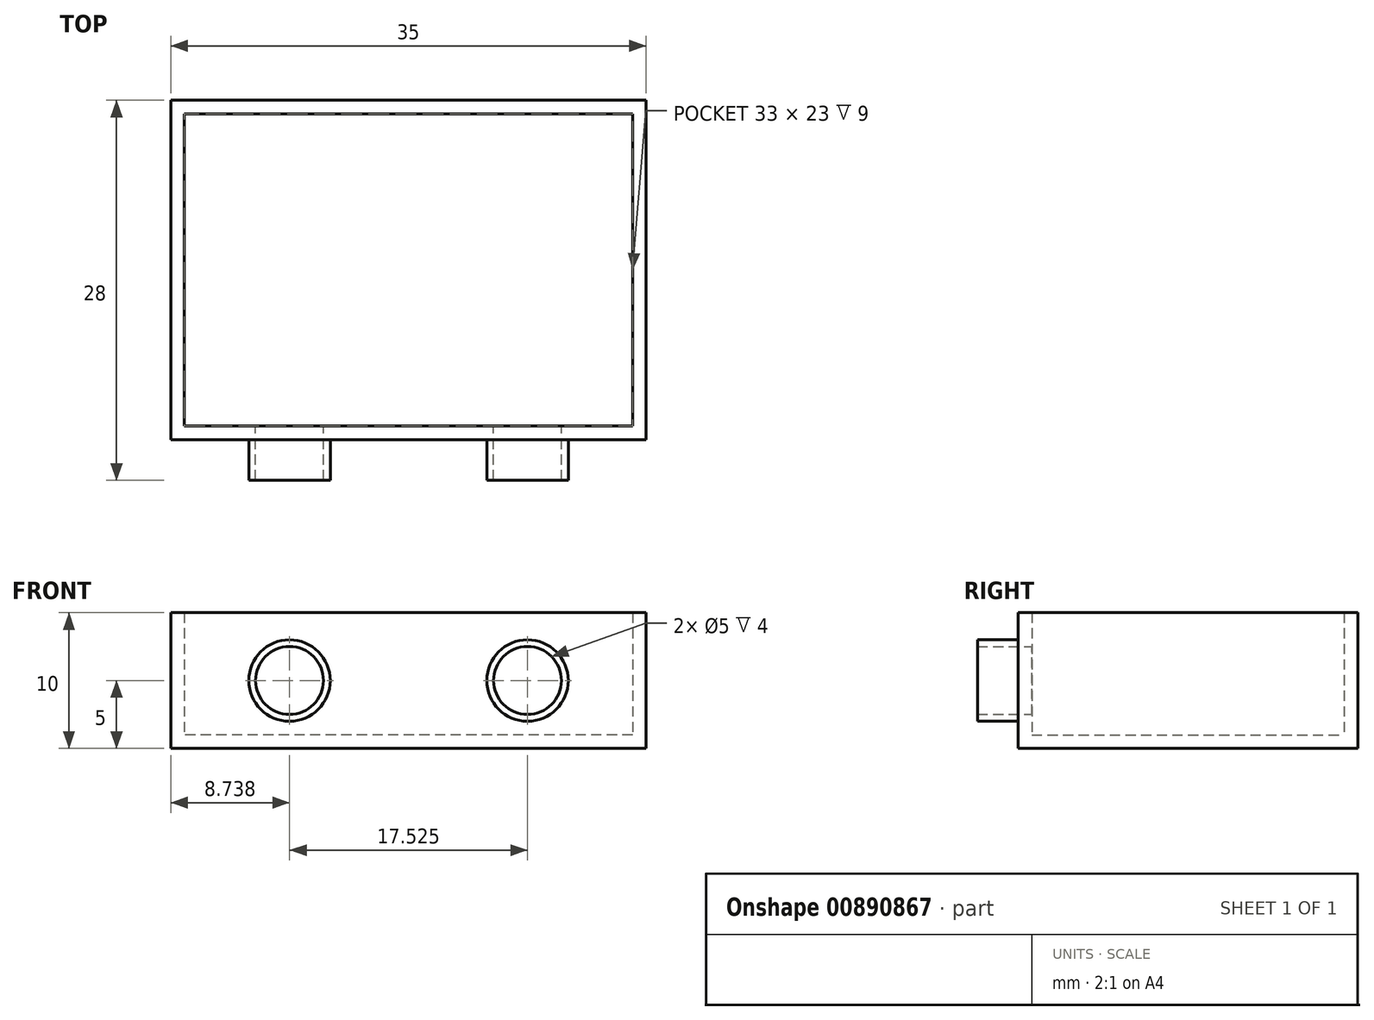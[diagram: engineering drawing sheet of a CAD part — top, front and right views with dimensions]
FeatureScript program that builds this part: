
annotation { "Feature Type Name" : "Feature", "Feature Type Description" : "" }
export const myFeature = defineFeature(function(context is Context, id is Id, definition is map)
    precondition{}
    {
        {
            var Q0;
            Q0=qCreatedBy(makeId("Top.planeOp"),FACE);
            var sketch = newSketch(context, id + "F0", { "sketchPlane" : qUnion([Q0])});
            skLineSegment(sketch, "E0.bottom", {"start": v(-2.95, 0) * mm, "end": v(-37.95, 0) * mm});
            skLineSegment(sketch, "E0.top", {"start": v(-2.95, 25) * mm, "end": v(-37.95, 25) * mm});
            skLineSegment(sketch, "E0.left", {"start": v(-2.95, 0) * mm, "end": v(-2.95, 25) * mm});
            skLineSegment(sketch, "E0.right", {"start": v(-37.95, 0) * mm, "end": v(-37.95, 25) * mm});
            skPoint(sketch, "E0.middle", {"position": v(-20.45, 12.5) * mm});
            skSolve(sketch);
        }
        {
            var Q0;
            Q0=makeQuery(id+"F0.imprint","IMPRINT",FACE,{"disambiguationData":[TD([[makeQuery(id+"F0.imprint","IMPRINT",EDGE,{"derivedFrom":sQuery(id+"F0.wireOp",EDGE,"E0.bottom")}),-1.0]])]});
            extrude(context, id + "F1", {"entities" : qUnion([Q0]), "depth" : 10 * mm, "offsetDistance" : 25.4 * mm});
        }
        {
            var Q0;
            Q0=makeQuery(id+"F1.opExtrude","SWEPT_FACE",FACE,{"disambiguationData":[OSD([sQuery(id+"F0.wireOp",EDGE,"E0.bottom")])]});
            var sketch = newSketch(context, id + "F2", { "sketchPlane" : qUnion([Q0])});
            skCircle(sketch, "E1", {"center": v(-29.21, 5) * mm, "radius": 3 * mm});
            skCircle(sketch, "E2", {"center": v(-11.69, 5) * mm, "radius": 3 * mm});
            skLineSegment(sketch, "E3", {"start": v(-37.95, 5) * mm, "end": v(-2.95, 5) * mm, "construction": true});
            skCircle(sketch, "E4", {"center": v(-29.21, 5) * mm, "radius": 2.5 * mm});
            skCircle(sketch, "E5", {"center": v(-11.69, 5) * mm, "radius": 2.5 * mm});
            skSolve(sketch);
        }
        {
            var Q0;
            Q0=makeQuery(id+"F1.opExtrude","CAP_FACE",FACE,{"disambiguationData":[OSD([sQuery(id+"F0.wireOp",EDGE,"E0.bottom"),sQuery(id+"F0.wireOp",EDGE,"E0.top"),sQuery(id+"F0.wireOp",EDGE,"E0.left"),sQuery(id+"F0.wireOp",EDGE,"E0.right")])],"isStart":false});
            shell(context, id + "F3", {"entities" : qUnion([Q0]), "thickness" : 1 * mm});
        }
        {
            var Q0;
            Q0=makeQuery(id+"F2.imprint","IMPRINT",FACE,{"disambiguationData":[TD([[makeQuery(id+"F2.imprint","IMPRINT",EDGE,{"derivedFrom":sQuery(id+"F2.wireOp",EDGE,"E1")}),1.0]])]});
            var Q1;
            Q1=makeQuery(id+"F2.imprint","IMPRINT",FACE,{"disambiguationData":[TD([[makeQuery(id+"F2.imprint","IMPRINT",EDGE,{"derivedFrom":sQuery(id+"F2.wireOp",EDGE,"E2")}),1.0]])]});
            var Q2;
            Q2=sQuery(id+"F2.wireOp",EDGE,"E1");
            var Q3;
            Q3=sQuery(id+"F2.wireOp",EDGE,"E4");
            var Q4;
            Q4=sQuery(id+"F2.wireOp",EDGE,"E5");
            var Q5;
            Q5=sQuery(id+"F2.wireOp",EDGE,"E2");
            extrude(context, id + "F4", {"entities" : qUnion([Q0, Q1]), "operationType" : NewBodyOperationType.ADD, "surfaceEntities" : qUnion([Q2, Q3, Q4, Q5]), "depth" : 3 * mm, "offsetDistance" : 25.4 * mm});
        }
        {
            var Q0;
            Q0=makeQuery(id+"F4.boolean.opBoolean","SPLIT",FACE,{"disambiguationData":[TD([makeQuery(id+"F4.opExtrude","SWEPT_FACE",FACE,{"disambiguationData":[OSD([sQuery(id+"F2.wireOp",EDGE,"E4")])]})])],"derivedFrom":makeQuery(id+"F1.opExtrude","SWEPT_FACE",FACE,{"disambiguationData":[OSD([sQuery(id+"F0.wireOp",EDGE,"E0.bottom")])]})});
            var Q1;
            Q1=makeQuery(id+"F4.boolean.opBoolean","SPLIT",FACE,{"disambiguationData":[TD([makeQuery(id+"F4.opExtrude","SWEPT_FACE",FACE,{"disambiguationData":[OSD([sQuery(id+"F2.wireOp",EDGE,"E5")])]})])],"derivedFrom":makeQuery(id+"F1.opExtrude","SWEPT_FACE",FACE,{"disambiguationData":[OSD([sQuery(id+"F0.wireOp",EDGE,"E0.bottom")])]})});
            extrude(context, id + "F5", {"entities" : qUnion([Q0, Q1]), "operationType" : NewBodyOperationType.REMOVE, "oppositeDirection" : true, "depth" : 1 * mm, "offsetDistance" : 25.4 * mm});
        }
    });
